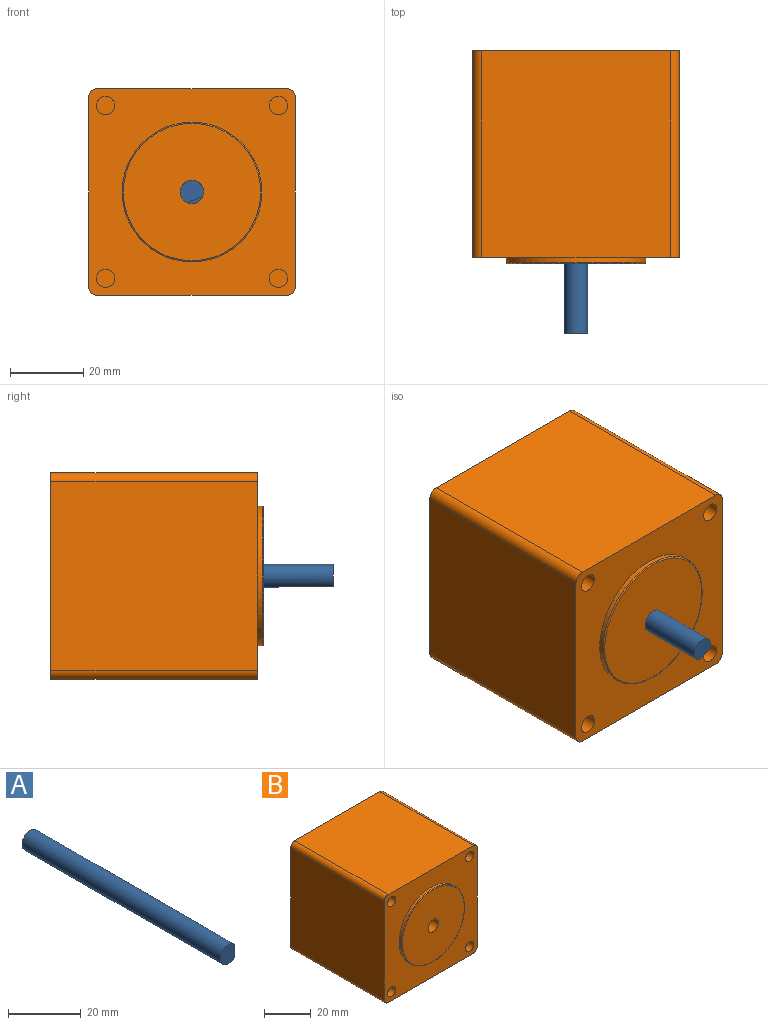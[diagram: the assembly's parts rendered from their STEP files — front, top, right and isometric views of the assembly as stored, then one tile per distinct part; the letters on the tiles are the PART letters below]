
ASSEMBLY  parts=2 mates=1
PART A: 5 faces, bbox 6.4x77x6.4 mm
  f0: plane 6.35x5.35mm, normal (0,-1,0), area 28.5mm2, adj f2,f3
  f1: plane 6.35x6.35mm, normal (0,1,0), area 31.7mm2, adj f2
  f2: cylinder r=3.17mm len=77mm, axis (0,1,0), area 1458.3mm2, adj f0,f1,f3,f4
  f3: plane 15x4.63mm, normal (1,0,0), area 69.4mm2, adj f0,f2,f4
  f4: plane 4.63x1mm, normal (0,-1,0), area 3.2mm2, adj f2,f3
PART B: 22 faces, bbox 56.4x58x56.4 mm
  f0: plane 56.4x51.4mm, normal (0,0,-1), area 2899mm2, adj f5,f6,f18,f21
  f1: plane 56.4x51.4mm, normal (1,0,0), area 2899mm2, adj f5,f6,f18,f19
  f2: plane 56.4x51.4mm, normal (0,0,1), area 2899mm2, adj f5,f6,f19,f20
  f3: cylinder r=3.17mm len=58mm, axis (0,-1,0), area 1157mm2, adj f5,f8
  f4: plane 56.4x51.4mm, normal (-1,0,0), area 2899mm2, adj f5,f6,f20,f21
  f5: plane 56.4x56.4mm, normal (0,1,0), area 3143.9mm2, adj f0,f1,f2,f3,f4,f18,f19,f20
  f6: plane 56.4x56.4mm, normal (0,-1,0), area 1957mm2, adj f0,f1,f2,f4,f7,f9,f11,f13
  f7: cylinder r=19.05mm len=38.1mm, axis (0,1,0), area 153.2mm2, adj f6,f17
  f8: plane 37.46x37.46mm, normal (0,-1,0), area 1070.4mm2, adj f3,f17
  f9: cylinder r=2.5mm len=10mm, axis (0,-1,0), area 157.1mm2, adj f6,f10
  f10: plane 5x5mm, normal (0,-1,0), area 19.6mm2, adj f9
  f11: cylinder r=2.5mm len=10mm, axis (0,-1,0), area 157.1mm2, adj f6,f12
  f12: plane 5x5mm, normal (0,-1,0), area 19.6mm2, adj f11
  f13: cylinder r=2.5mm len=10mm, axis (0,-1,0), area 157.1mm2, adj f6,f14
  f14: plane 5x5mm, normal (0,-1,0), area 19.6mm2, adj f13
  f15: cylinder r=2.5mm len=10mm, axis (0,-1,0), area 157.1mm2, adj f6,f16
  f16: plane 5x5mm, normal (0,-1,0), area 19.6mm2, adj f15
  f17: torus R=18.73mm, axis (0,-1,0), area 59.8mm2, adj f7,f8
  f18: cylinder r=2.5mm len=56.4mm, axis (0,1,0), area 221.5mm2, adj f0,f1,f5,f6
  f19: cylinder r=2.5mm len=56.4mm, axis (0,-1,0), area 221.5mm2, adj f1,f2,f5,f6
  f20: cylinder r=2.5mm len=56.4mm, axis (0,1,0), area 221.5mm2, adj f2,f4,f5,f6
  f21: cylinder r=2.5mm len=56.4mm, axis (0,-1,0), area 221.5mm2, adj f0,f4,f5,f6
PLACE A rot(axis=(0,1,0),68.4deg) t=(0.27,0.2,0.01)mm
PLACE B t=(0.27,0.2,0.01)mm fixed
MATE revolute B.f3 <-> A.f2  axis (0,-1,0) through (0.27,56.6,0.01)mm
